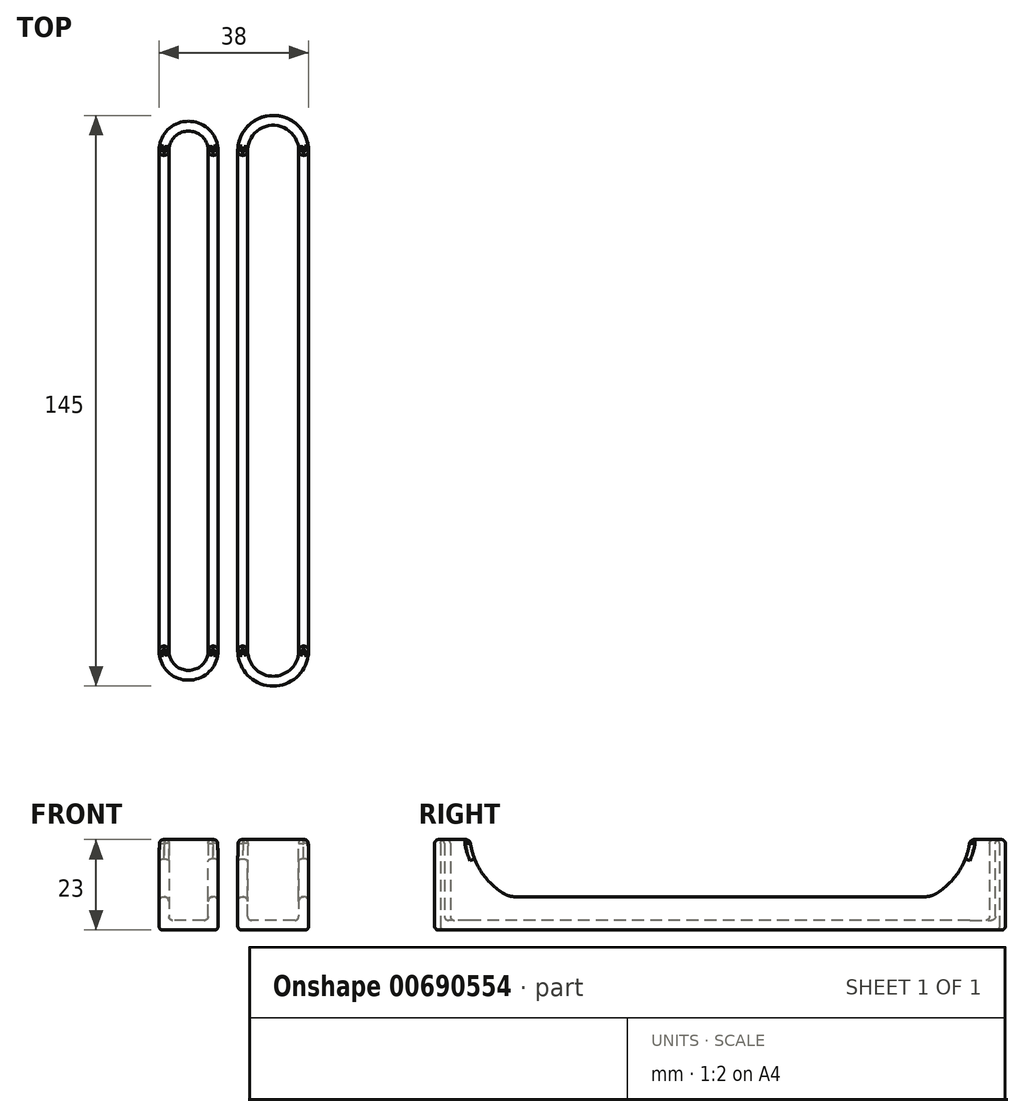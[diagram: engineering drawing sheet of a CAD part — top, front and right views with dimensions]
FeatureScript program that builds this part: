
annotation { "Feature Type Name" : "Feature", "Feature Type Description" : "" }
export const myFeature = defineFeature(function(context is Context, id is Id, definition is map)
    precondition{}
    {
        {
            var Q0;
            Q0=qCreatedBy(makeId("Top.planeOp"),FACE);
            var sketch = newSketch(context, id + "F0", { "sketchPlane" : qUnion([Q0])});
            skLineSegment(sketch, "E0.left", {"start": v(-27.24, 46.28) * mm, "end": v(-27.24, -80.72) * mm});
            skLineSegment(sketch, "E0.right", {"start": v(-12.24, 46.28) * mm, "end": v(-12.24, -80.72) * mm});
            skLineSegment(sketch, "E1.left", {"start": v(-7.24, 46.28) * mm, "end": v(-7.24, -80.72) * mm});
            skLineSegment(sketch, "E1.right", {"start": v(10.76, 46.28) * mm, "end": v(10.76, -80.72) * mm});
            skArc(sketch, "E2", {"start": v(-27.24, -80.72) * mm, "mid": v(-19.74, -88.22) * mm, "end": v(-12.24, -80.72) * mm});
            skArc(sketch, "E3", {"start": v(-12.24, 46.28) * mm, "mid": v(-19.74, 53.78) * mm, "end": v(-27.24, 46.28) * mm});
            skArc(sketch, "E4", {"start": v(10.76, 46.28) * mm, "mid": v(1.76, 55.28) * mm, "end": v(-7.24, 46.28) * mm});
            skArc(sketch, "E5", {"start": v(-7.24, -80.72) * mm, "mid": v(1.76, -89.72) * mm, "end": v(10.76, -80.72) * mm});
            skSolve(sketch);
        }
        {
            var Q0;
            Q0=makeQuery(id+"F0.imprint","IMPRINT",FACE,{"disambiguationData":[TD([[makeQuery(id+"F0.imprint","IMPRINT",EDGE,{"derivedFrom":sQuery(id+"F0.wireOp",EDGE,"E1.left")}),1.0]])]});
            var Q1;
            Q1=makeQuery(id+"F0.imprint","IMPRINT",FACE,{"disambiguationData":[TD([[makeQuery(id+"F0.imprint","IMPRINT",EDGE,{"derivedFrom":sQuery(id+"F0.wireOp",EDGE,"E0.left")}),1.0]])]});
            extrude(context, id + "F1", {"entities" : qUnion([Q0, Q1]), "depth" : 23 * mm, "offsetDistance" : 25 * mm});
        }
        {
            var Q0;
            Q0=makeQuery(id+"F1.opExtrude","CAP_FACE",FACE,{"disambiguationData":[OSD([sQuery(id+"F0.wireOp",EDGE,"E0.left"),sQuery(id+"F0.wireOp",EDGE,"E0.right"),sQuery(id+"F0.wireOp",EDGE,"E2"),sQuery(id+"F0.wireOp",EDGE,"E3")])],"isStart":false});
            var Q1;
            Q1=makeQuery(id+"F1.opExtrude","CAP_FACE",FACE,{"disambiguationData":[OSD([sQuery(id+"F0.wireOp",EDGE,"E1.left"),sQuery(id+"F0.wireOp",EDGE,"E1.right"),sQuery(id+"F0.wireOp",EDGE,"E4"),sQuery(id+"F0.wireOp",EDGE,"E5")])],"isStart":false});
            shell(context, id + "F2", {"entities" : qUnion([Q0, Q1]), "thickness" : 2.5 * mm});
        }
        {
            var Q0;
            Q0=makeQuery(id+"F1.opExtrude","CAP_EDGE",EDGE,{"disambiguationData":[OSD([sQuery(id+"F0.wireOp",EDGE,"E2")])],"isStart":false});
            var Q1;
            Q1=makeQuery(id+"F1.opExtrude","CAP_EDGE",EDGE,{"disambiguationData":[OSD([sQuery(id+"F0.wireOp",EDGE,"E0.right")])],"isStart":true});
            var Q2;
            Q2=makeQuery(id+"F1.opExtrude","CAP_EDGE",EDGE,{"disambiguationData":[OSD([sQuery(id+"F0.wireOp",EDGE,"E0.right")])],"isStart":false});
            var Q3;
            {var subQ0=sQuery(id+"F0.wireOp",EDGE,"E0.right");Q3=makeQuery(id+"F2.opShell","OFFSET_EDGE",EDGE,{"disambiguationData":[OSD([subQ0]),TDD([makeQuery(id+"F1.opExtrude","CAP_EDGE",EDGE,{"disambiguationData":[OSD([subQ0])],"isStart":false})])]});}
            var Q4;
            {var subQ0=sQuery(id+"F0.wireOp",EDGE,"E2");Q4=makeQuery(id+"F2.opShell","OFFSET_EDGE",EDGE,{"disambiguationData":[OSD([subQ0]),TDD([makeQuery(id+"F1.opExtrude","CAP_EDGE",EDGE,{"disambiguationData":[OSD([subQ0])],"isStart":false})])]});}
            var Q5;
            {var subQ0=sQuery(id+"F0.wireOp",EDGE,"E0.left");Q5=makeQuery(id+"F2.opShell","OFFSET_EDGE",EDGE,{"disambiguationData":[OSD([subQ0]),TDD([makeQuery(id+"F1.opExtrude","CAP_EDGE",EDGE,{"disambiguationData":[OSD([subQ0])],"isStart":false})])]});}
            var Q6;
            Q6=makeQuery(id+"F1.opExtrude","CAP_EDGE",EDGE,{"disambiguationData":[OSD([sQuery(id+"F0.wireOp",EDGE,"E0.left")])],"isStart":false});
            var Q7;
            {var subQ0=sQuery(id+"F0.wireOp",EDGE,"E3");Q7=makeQuery(id+"F2.opShell","OFFSET_EDGE",EDGE,{"disambiguationData":[OSD([subQ0]),TDD([makeQuery(id+"F1.opExtrude","CAP_EDGE",EDGE,{"disambiguationData":[OSD([subQ0])],"isStart":false})])]});}
            var Q8;
            Q8=makeQuery(id+"F1.opExtrude","CAP_EDGE",EDGE,{"disambiguationData":[OSD([sQuery(id+"F0.wireOp",EDGE,"E3")])],"isStart":false});
            var Q9;
            Q9=makeQuery(id+"F1.opExtrude","CAP_EDGE",EDGE,{"disambiguationData":[OSD([sQuery(id+"F0.wireOp",EDGE,"E3")])],"isStart":true});
            var Q10;
            Q10=makeQuery(id+"F1.opExtrude","CAP_EDGE",EDGE,{"disambiguationData":[OSD([sQuery(id+"F0.wireOp",EDGE,"E0.left")])],"isStart":true});
            var Q11;
            Q11=makeQuery(id+"F1.opExtrude","CAP_EDGE",EDGE,{"disambiguationData":[OSD([sQuery(id+"F0.wireOp",EDGE,"E2")])],"isStart":true});
            var Q12;
            {var subQ0=sQuery(id+"F0.wireOp",EDGE,"E1.left");Q12=makeQuery(id+"F2.opShell","OFFSET_EDGE",EDGE,{"disambiguationData":[OSD([subQ0]),TDD([makeQuery(id+"F1.opExtrude","CAP_EDGE",EDGE,{"disambiguationData":[OSD([subQ0])],"isStart":false})])]});}
            var Q13;
            Q13=makeQuery(id+"F1.opExtrude","CAP_EDGE",EDGE,{"disambiguationData":[OSD([sQuery(id+"F0.wireOp",EDGE,"E1.left")])],"isStart":false});
            var Q14;
            {var subQ0=sQuery(id+"F0.wireOp",EDGE,"E1.right");Q14=makeQuery(id+"F2.opShell","OFFSET_EDGE",EDGE,{"disambiguationData":[OSD([subQ0]),TDD([makeQuery(id+"F1.opExtrude","CAP_EDGE",EDGE,{"disambiguationData":[OSD([subQ0])],"isStart":false})])]});}
            var Q15;
            Q15=makeQuery(id+"F1.opExtrude","CAP_EDGE",EDGE,{"disambiguationData":[OSD([sQuery(id+"F0.wireOp",EDGE,"E1.right")])],"isStart":false});
            var Q16;
            Q16=makeQuery(id+"F1.opExtrude","CAP_EDGE",EDGE,{"disambiguationData":[OSD([sQuery(id+"F0.wireOp",EDGE,"E5")])],"isStart":false});
            var Q17;
            {var subQ0=sQuery(id+"F0.wireOp",EDGE,"E5");Q17=makeQuery(id+"F2.opShell","OFFSET_EDGE",EDGE,{"disambiguationData":[OSD([subQ0]),TDD([makeQuery(id+"F1.opExtrude","CAP_EDGE",EDGE,{"disambiguationData":[OSD([subQ0])],"isStart":false})])]});}
            var Q18;
            {var subQ0=sQuery(id+"F0.wireOp",EDGE,"E4");Q18=makeQuery(id+"F2.opShell","OFFSET_EDGE",EDGE,{"disambiguationData":[OSD([subQ0]),TDD([makeQuery(id+"F1.opExtrude","CAP_EDGE",EDGE,{"disambiguationData":[OSD([subQ0])],"isStart":false})])]});}
            var Q19;
            Q19=makeQuery(id+"F1.opExtrude","CAP_EDGE",EDGE,{"disambiguationData":[OSD([sQuery(id+"F0.wireOp",EDGE,"E4")])],"isStart":false});
            var Q20;
            Q20=makeQuery(id+"F1.opExtrude","CAP_EDGE",EDGE,{"disambiguationData":[OSD([sQuery(id+"F0.wireOp",EDGE,"E5")])],"isStart":true});
            var Q21;
            Q21=makeQuery(id+"F1.opExtrude","CAP_EDGE",EDGE,{"disambiguationData":[OSD([sQuery(id+"F0.wireOp",EDGE,"E1.right")])],"isStart":true});
            var Q22;
            Q22=makeQuery(id+"F1.opExtrude","CAP_EDGE",EDGE,{"disambiguationData":[OSD([sQuery(id+"F0.wireOp",EDGE,"E4")])],"isStart":true});
            var Q23;
            Q23=makeQuery(id+"F1.opExtrude","CAP_EDGE",EDGE,{"disambiguationData":[OSD([sQuery(id+"F0.wireOp",EDGE,"E1.left")])],"isStart":true});
            var Q24;
            {var subQ0=sQuery(id+"F0.wireOp",EDGE,"E1.left");Q24=makeQuery(id+"F2.opShell","OFFSET_EDGE",EDGE,{"disambiguationData":[OSD([subQ0]),TDD([makeQuery(id+"F1.opExtrude","CAP_EDGE",EDGE,{"disambiguationData":[OSD([subQ0])],"isStart":true})])]});}
            var Q25;
            {var subQ0=sQuery(id+"F0.wireOp",EDGE,"E4");Q25=makeQuery(id+"F2.opShell","OFFSET_EDGE",EDGE,{"disambiguationData":[OSD([subQ0]),TDD([makeQuery(id+"F1.opExtrude","CAP_EDGE",EDGE,{"disambiguationData":[OSD([subQ0])],"isStart":true})])]});}
            var Q26;
            {var subQ0=sQuery(id+"F0.wireOp",EDGE,"E1.right");Q26=makeQuery(id+"F2.opShell","OFFSET_EDGE",EDGE,{"disambiguationData":[OSD([subQ0]),TDD([makeQuery(id+"F1.opExtrude","CAP_EDGE",EDGE,{"disambiguationData":[OSD([subQ0])],"isStart":true})])]});}
            var Q27;
            {var subQ0=sQuery(id+"F0.wireOp",EDGE,"E5");Q27=makeQuery(id+"F2.opShell","OFFSET_EDGE",EDGE,{"disambiguationData":[OSD([subQ0]),TDD([makeQuery(id+"F1.opExtrude","CAP_EDGE",EDGE,{"disambiguationData":[OSD([subQ0])],"isStart":true})])]});}
            var Q28;
            {var subQ0=sQuery(id+"F0.wireOp",EDGE,"E2");Q28=makeQuery(id+"F2.opShell","OFFSET_EDGE",EDGE,{"disambiguationData":[OSD([subQ0]),TDD([makeQuery(id+"F1.opExtrude","CAP_EDGE",EDGE,{"disambiguationData":[OSD([subQ0])],"isStart":true})])]});}
            var Q29;
            {var subQ0=sQuery(id+"F0.wireOp",EDGE,"E0.right");Q29=makeQuery(id+"F2.opShell","OFFSET_EDGE",EDGE,{"disambiguationData":[OSD([subQ0]),TDD([makeQuery(id+"F1.opExtrude","CAP_EDGE",EDGE,{"disambiguationData":[OSD([subQ0])],"isStart":true})])]});}
            var Q30;
            {var subQ0=sQuery(id+"F0.wireOp",EDGE,"E3");Q30=makeQuery(id+"F2.opShell","OFFSET_EDGE",EDGE,{"disambiguationData":[OSD([subQ0]),TDD([makeQuery(id+"F1.opExtrude","CAP_EDGE",EDGE,{"disambiguationData":[OSD([subQ0])],"isStart":true})])]});}
            var Q31;
            {var subQ0=sQuery(id+"F0.wireOp",EDGE,"E0.left");Q31=makeQuery(id+"F2.opShell","OFFSET_EDGE",EDGE,{"disambiguationData":[OSD([subQ0]),TDD([makeQuery(id+"F1.opExtrude","CAP_EDGE",EDGE,{"disambiguationData":[OSD([subQ0])],"isStart":true})])]});}
            fillet(context, id + "F3", {"entities" : qUnion([Q0, Q1, Q2, Q3, Q4, Q5, Q6, Q7, Q8, Q9, Q10, Q11, Q12, Q13, Q14, Q15, Q16, Q17, Q18, Q19, Q20, Q21, Q22, Q23, Q24, Q25, Q26, Q27, Q28, Q29, Q30, Q31]), "radius" : 1 * mm, "tangentPropagation" : true, "allowEdgeOverflow" : false});
        }
        {
            var Q0;
            Q0=makeQuery(id+"F1.opExtrude","SWEPT_FACE",FACE,{"disambiguationData":[OSD([sQuery(id+"F0.wireOp",EDGE,"E1.right")])]});
            var sketch = newSketch(context, id + "F4", { "sketchPlane" : qUnion([Q0])});
            skLineSegment(sketch, "E6", {"start": v(-80.72, 23) * mm, "end": v(46.28, 23) * mm});
            skLineSegment(sketch, "E7", {"start": v(35.02, 8.5) * mm, "end": v(-69.46, 8.5) * mm});
            skArc(sketch, "E8", {"start": v(-80.72, 23) * mm, "mid": v(-78.02, 15.06) * mm, "end": v(-72.02, 9.2) * mm});
            skArc(sketch, "E9", {"start": v(37.59, 9.2) * mm, "mid": v(43.59, 15.06) * mm, "end": v(46.28, 23) * mm});
            skPoint(sketch, "E10.visualSharp", {"position": v(-70.72, 8.5) * mm});
            skArc(sketch, "E10.filletArc", {"start": v(-72.02, 9.2) * mm, "mid": v(-70.79, 8.68) * mm, "end": v(-69.46, 8.5) * mm});
            skPoint(sketch, "E11.visualSharp", {"position": v(36.28, 8.5) * mm});
            skArc(sketch, "E11.filletArc", {"start": v(35.02, 8.5) * mm, "mid": v(36.35, 8.68) * mm, "end": v(37.59, 9.2) * mm});
            skSolve(sketch);
        }
        {
            var Q0;
            Q0 = qSketchRegion(id + "F4", true);
            extrude(context, id + "F5", {"entities" : qUnion([Q0]), "operationType" : NewBodyOperationType.REMOVE, "oppositeDirection" : true, "depth" : 70.7 * mm, "offsetDistance" : 25 * mm});
        }
        {
            var Q0;
            {var subQ0=sQuery(id+"F0.wireOp",EDGE,"E1.right");var subQ1=makeQuery(id+"F1.opExtrude","CAP_EDGE",EDGE,{"disambiguationData":[OSD([subQ0])],"isStart":false});var subQ2=sQuery(id+"F0.wireOp",EDGE,"E5");var subQ4=makeQuery(id+"F1.opExtrude","CAP_FACE",FACE,{"disambiguationData":[OSD([sQuery(id+"F0.wireOp",EDGE,"E1.left"),subQ0,sQuery(id+"F0.wireOp",EDGE,"E4"),subQ2])],"isStart":false});var subQ5=sQuery(id+"F4.wireOp",EDGE,"E8");var subQ6=makeQuery(id+"F5.opExtrude","SWEPT_FACE",FACE,{"disambiguationData":[OSD([subQ5])]});Q0=makeQuery(id+"F5.boolean.opBoolean","COPY",EDGE,{"disambiguationData":[topologyDisambiguationEdgeConnected([subQ4,subQ6]),TD([makeQuery(id+"F3.opFillet","BLEND_FACE",FACE,{"disambiguationData":[OSD([subQ0]),TDD([subQ1])]})])],"derivedFrom":makeQuery(id+"F5.opExtrude","SWEPT_EDGE",EDGE,{"disambiguationData":[OSD([sQuery(id+"F4.wireOp",EDGE,"E6"),subQ5])]})});}
            var Q1;
            {var subQ0=sQuery(id+"F0.wireOp",EDGE,"E1.right");Q1=makeQuery(id+"F5.boolean.opBoolean","INTERSECT",EDGE,{"derivedFrom":[makeQuery(id+"F3.opFillet","BLEND_FACE",FACE,{"disambiguationData":[OSD([subQ0]),TDD([makeQuery(id+"F1.opExtrude","CAP_EDGE",EDGE,{"disambiguationData":[OSD([subQ0])],"isStart":false})])]}),makeQuery(id+"F5.opExtrude","SWEPT_FACE",FACE,{"disambiguationData":[OSD([sQuery(id+"F4.wireOp",EDGE,"E8")])]})]});}
            var Q2;
            {var subQ0=sQuery(id+"F0.wireOp",EDGE,"E1.right");Q2=makeQuery(id+"F5.boolean.opBoolean","INTERSECT",EDGE,{"derivedFrom":[makeQuery(id+"F3.opFillet","BLEND_FACE",FACE,{"disambiguationData":[OSD([subQ0]),TDD([makeQuery(id+"F2.opShell","OFFSET_EDGE",EDGE,{"disambiguationData":[OSD([subQ0]),TDD([makeQuery(id+"F1.opExtrude","CAP_EDGE",EDGE,{"disambiguationData":[OSD([subQ0])],"isStart":false})])]})])]}),makeQuery(id+"F5.opExtrude","SWEPT_FACE",FACE,{"disambiguationData":[OSD([sQuery(id+"F4.wireOp",EDGE,"E8")])]})]});}
            var Q3;
            {var subQ0=sQuery(id+"F0.wireOp",EDGE,"E1.left");Q3=makeQuery(id+"F5.boolean.opBoolean","INTERSECT",EDGE,{"derivedFrom":[makeQuery(id+"F3.opFillet","BLEND_FACE",FACE,{"disambiguationData":[OSD([subQ0]),TDD([makeQuery(id+"F2.opShell","OFFSET_EDGE",EDGE,{"disambiguationData":[OSD([subQ0]),TDD([makeQuery(id+"F1.opExtrude","CAP_EDGE",EDGE,{"disambiguationData":[OSD([subQ0])],"isStart":false})])]})])]}),makeQuery(id+"F5.opExtrude","SWEPT_FACE",FACE,{"disambiguationData":[OSD([sQuery(id+"F4.wireOp",EDGE,"E8")])]})]});}
            var Q4;
            {var subQ0=sQuery(id+"F0.wireOp",EDGE,"E1.left");var subQ1=makeQuery(id+"F1.opExtrude","CAP_EDGE",EDGE,{"disambiguationData":[OSD([subQ0])],"isStart":false});var subQ2=sQuery(id+"F0.wireOp",EDGE,"E5");var subQ4=sQuery(id+"F4.wireOp",EDGE,"E8");var subQ5=makeQuery(id+"F5.opExtrude","SWEPT_FACE",FACE,{"disambiguationData":[OSD([subQ4])]});var subQ6=makeQuery(id+"F1.opExtrude","CAP_FACE",FACE,{"disambiguationData":[OSD([subQ0,sQuery(id+"F0.wireOp",EDGE,"E1.right"),sQuery(id+"F0.wireOp",EDGE,"E4"),subQ2])],"isStart":false});Q4=makeQuery(id+"F5.boolean.opBoolean","COPY",EDGE,{"disambiguationData":[topologyDisambiguationEdgeConnected([subQ6,subQ5]),TD([makeQuery(id+"F3.opFillet","BLEND_FACE",FACE,{"disambiguationData":[OSD([subQ0]),TDD([subQ1])]})])],"derivedFrom":makeQuery(id+"F5.opExtrude","SWEPT_EDGE",EDGE,{"disambiguationData":[OSD([sQuery(id+"F4.wireOp",EDGE,"E6"),subQ4])]})});}
            var Q5;
            {var subQ0=sQuery(id+"F0.wireOp",EDGE,"E1.left");Q5=makeQuery(id+"F5.boolean.opBoolean","INTERSECT",EDGE,{"derivedFrom":[makeQuery(id+"F3.opFillet","BLEND_FACE",FACE,{"disambiguationData":[OSD([subQ0]),TDD([makeQuery(id+"F1.opExtrude","CAP_EDGE",EDGE,{"disambiguationData":[OSD([subQ0])],"isStart":false})])]}),makeQuery(id+"F5.opExtrude","SWEPT_FACE",FACE,{"disambiguationData":[OSD([sQuery(id+"F4.wireOp",EDGE,"E8")])]})]});}
            var Q6;
            {var subQ0=sQuery(id+"F0.wireOp",EDGE,"E0.right");var subQ1=makeQuery(id+"F1.opExtrude","CAP_EDGE",EDGE,{"disambiguationData":[OSD([subQ0])],"isStart":false});var subQ2=sQuery(id+"F0.wireOp",EDGE,"E2");var subQ4=makeQuery(id+"F1.opExtrude","CAP_FACE",FACE,{"disambiguationData":[OSD([sQuery(id+"F0.wireOp",EDGE,"E0.left"),subQ0,subQ2,sQuery(id+"F0.wireOp",EDGE,"E3")])],"isStart":false});var subQ5=sQuery(id+"F4.wireOp",EDGE,"E8");var subQ6=makeQuery(id+"F5.opExtrude","SWEPT_FACE",FACE,{"disambiguationData":[OSD([subQ5])]});Q6=makeQuery(id+"F5.boolean.opBoolean","COPY",EDGE,{"disambiguationData":[topologyDisambiguationEdgeConnected([subQ4,subQ6]),TD([makeQuery(id+"F3.opFillet","BLEND_FACE",FACE,{"disambiguationData":[OSD([subQ0]),TDD([subQ1])]})])],"derivedFrom":makeQuery(id+"F5.opExtrude","SWEPT_EDGE",EDGE,{"disambiguationData":[OSD([sQuery(id+"F4.wireOp",EDGE,"E6"),subQ5])]})});}
            var Q7;
            {var subQ0=sQuery(id+"F0.wireOp",EDGE,"E0.right");Q7=makeQuery(id+"F5.boolean.opBoolean","INTERSECT",EDGE,{"derivedFrom":[makeQuery(id+"F3.opFillet","BLEND_FACE",FACE,{"disambiguationData":[OSD([subQ0]),TDD([makeQuery(id+"F1.opExtrude","CAP_EDGE",EDGE,{"disambiguationData":[OSD([subQ0])],"isStart":false})])]}),makeQuery(id+"F5.opExtrude","SWEPT_FACE",FACE,{"disambiguationData":[OSD([sQuery(id+"F4.wireOp",EDGE,"E8")])]})]});}
            var Q8;
            {var subQ0=sQuery(id+"F0.wireOp",EDGE,"E0.right");Q8=makeQuery(id+"F5.boolean.opBoolean","INTERSECT",EDGE,{"derivedFrom":[makeQuery(id+"F3.opFillet","BLEND_FACE",FACE,{"disambiguationData":[OSD([subQ0]),TDD([makeQuery(id+"F2.opShell","OFFSET_EDGE",EDGE,{"disambiguationData":[OSD([subQ0]),TDD([makeQuery(id+"F1.opExtrude","CAP_EDGE",EDGE,{"disambiguationData":[OSD([subQ0])],"isStart":false})])]})])]}),makeQuery(id+"F5.opExtrude","SWEPT_FACE",FACE,{"disambiguationData":[OSD([sQuery(id+"F4.wireOp",EDGE,"E8")])]})]});}
            var Q9;
            {var subQ0=sQuery(id+"F0.wireOp",EDGE,"E0.left");var subQ1=makeQuery(id+"F1.opExtrude","CAP_EDGE",EDGE,{"disambiguationData":[OSD([subQ0])],"isStart":false});var subQ2=sQuery(id+"F0.wireOp",EDGE,"E2");var subQ4=makeQuery(id+"F1.opExtrude","CAP_FACE",FACE,{"disambiguationData":[OSD([subQ0,sQuery(id+"F0.wireOp",EDGE,"E0.right"),subQ2,sQuery(id+"F0.wireOp",EDGE,"E3")])],"isStart":false});var subQ5=sQuery(id+"F4.wireOp",EDGE,"E8");var subQ6=makeQuery(id+"F5.opExtrude","SWEPT_FACE",FACE,{"disambiguationData":[OSD([subQ5])]});Q9=makeQuery(id+"F5.boolean.opBoolean","COPY",EDGE,{"disambiguationData":[topologyDisambiguationEdgeConnected([subQ4,subQ6]),TD([makeQuery(id+"F3.opFillet","BLEND_FACE",FACE,{"disambiguationData":[OSD([subQ0]),TDD([subQ1])]})])],"derivedFrom":makeQuery(id+"F5.opExtrude","SWEPT_EDGE",EDGE,{"disambiguationData":[OSD([sQuery(id+"F4.wireOp",EDGE,"E6"),subQ5])]})});}
            var Q10;
            {var subQ0=sQuery(id+"F0.wireOp",EDGE,"E0.left");Q10=makeQuery(id+"F5.boolean.opBoolean","INTERSECT",EDGE,{"derivedFrom":[makeQuery(id+"F3.opFillet","BLEND_FACE",FACE,{"disambiguationData":[OSD([subQ0]),TDD([makeQuery(id+"F2.opShell","OFFSET_EDGE",EDGE,{"disambiguationData":[OSD([subQ0]),TDD([makeQuery(id+"F1.opExtrude","CAP_EDGE",EDGE,{"disambiguationData":[OSD([subQ0])],"isStart":false})])]})])]}),makeQuery(id+"F5.opExtrude","SWEPT_FACE",FACE,{"disambiguationData":[OSD([sQuery(id+"F4.wireOp",EDGE,"E8")])]})]});}
            var Q11;
            {var subQ0=sQuery(id+"F0.wireOp",EDGE,"E0.left");Q11=makeQuery(id+"F5.boolean.opBoolean","INTERSECT",EDGE,{"derivedFrom":[makeQuery(id+"F3.opFillet","BLEND_FACE",FACE,{"disambiguationData":[OSD([subQ0]),TDD([makeQuery(id+"F1.opExtrude","CAP_EDGE",EDGE,{"disambiguationData":[OSD([subQ0])],"isStart":false})])]}),makeQuery(id+"F5.opExtrude","SWEPT_FACE",FACE,{"disambiguationData":[OSD([sQuery(id+"F4.wireOp",EDGE,"E8")])]})]});}
            var Q12;
            {var subQ0=sQuery(id+"F0.wireOp",EDGE,"E0.left");Q12=makeQuery(id+"F5.boolean.opBoolean","INTERSECT",EDGE,{"derivedFrom":[makeQuery(id+"F3.opFillet","BLEND_FACE",FACE,{"disambiguationData":[OSD([subQ0]),TDD([makeQuery(id+"F1.opExtrude","CAP_EDGE",EDGE,{"disambiguationData":[OSD([subQ0])],"isStart":false})])]}),makeQuery(id+"F5.opExtrude","SWEPT_FACE",FACE,{"disambiguationData":[OSD([sQuery(id+"F4.wireOp",EDGE,"E9")])]})]});}
            var Q13;
            {var subQ0=sQuery(id+"F0.wireOp",EDGE,"E0.left");var subQ1=makeQuery(id+"F1.opExtrude","CAP_EDGE",EDGE,{"disambiguationData":[OSD([subQ0])],"isStart":false});var subQ2=sQuery(id+"F4.wireOp",EDGE,"E9");var subQ3=makeQuery(id+"F5.opExtrude","SWEPT_FACE",FACE,{"disambiguationData":[OSD([subQ2])]});var subQ4=sQuery(id+"F0.wireOp",EDGE,"E3");var subQ6=makeQuery(id+"F1.opExtrude","CAP_FACE",FACE,{"disambiguationData":[OSD([subQ0,sQuery(id+"F0.wireOp",EDGE,"E0.right"),sQuery(id+"F0.wireOp",EDGE,"E2"),subQ4])],"isStart":false});Q13=makeQuery(id+"F5.boolean.opBoolean","COPY",EDGE,{"disambiguationData":[topologyDisambiguationEdgeConnected([subQ6,subQ3]),TD([makeQuery(id+"F3.opFillet","BLEND_FACE",FACE,{"disambiguationData":[OSD([subQ0]),TDD([subQ1])]})])],"derivedFrom":makeQuery(id+"F5.opExtrude","SWEPT_EDGE",EDGE,{"disambiguationData":[OSD([sQuery(id+"F4.wireOp",EDGE,"E6"),subQ2])]})});}
            var Q14;
            {var subQ0=sQuery(id+"F0.wireOp",EDGE,"E0.left");Q14=makeQuery(id+"F5.boolean.opBoolean","INTERSECT",EDGE,{"derivedFrom":[makeQuery(id+"F3.opFillet","BLEND_FACE",FACE,{"disambiguationData":[OSD([subQ0]),TDD([makeQuery(id+"F2.opShell","OFFSET_EDGE",EDGE,{"disambiguationData":[OSD([subQ0]),TDD([makeQuery(id+"F1.opExtrude","CAP_EDGE",EDGE,{"disambiguationData":[OSD([subQ0])],"isStart":false})])]})])]}),makeQuery(id+"F5.opExtrude","SWEPT_FACE",FACE,{"disambiguationData":[OSD([sQuery(id+"F4.wireOp",EDGE,"E9")])]})]});}
            var Q15;
            {var subQ0=sQuery(id+"F0.wireOp",EDGE,"E0.right");Q15=makeQuery(id+"F5.boolean.opBoolean","INTERSECT",EDGE,{"derivedFrom":[makeQuery(id+"F3.opFillet","BLEND_FACE",FACE,{"disambiguationData":[OSD([subQ0]),TDD([makeQuery(id+"F2.opShell","OFFSET_EDGE",EDGE,{"disambiguationData":[OSD([subQ0]),TDD([makeQuery(id+"F1.opExtrude","CAP_EDGE",EDGE,{"disambiguationData":[OSD([subQ0])],"isStart":false})])]})])]}),makeQuery(id+"F5.opExtrude","SWEPT_FACE",FACE,{"disambiguationData":[OSD([sQuery(id+"F4.wireOp",EDGE,"E9")])]})]});}
            var Q16;
            {var subQ0=sQuery(id+"F0.wireOp",EDGE,"E0.right");var subQ1=makeQuery(id+"F1.opExtrude","CAP_EDGE",EDGE,{"disambiguationData":[OSD([subQ0])],"isStart":false});var subQ2=sQuery(id+"F0.wireOp",EDGE,"E3");var subQ4=makeQuery(id+"F1.opExtrude","CAP_FACE",FACE,{"disambiguationData":[OSD([sQuery(id+"F0.wireOp",EDGE,"E0.left"),subQ0,sQuery(id+"F0.wireOp",EDGE,"E2"),subQ2])],"isStart":false});var subQ5=sQuery(id+"F4.wireOp",EDGE,"E9");var subQ6=makeQuery(id+"F5.opExtrude","SWEPT_FACE",FACE,{"disambiguationData":[OSD([subQ5])]});Q16=makeQuery(id+"F5.boolean.opBoolean","COPY",EDGE,{"disambiguationData":[topologyDisambiguationEdgeConnected([subQ4,subQ6]),TD([makeQuery(id+"F3.opFillet","BLEND_FACE",FACE,{"disambiguationData":[OSD([subQ0]),TDD([subQ1])]})])],"derivedFrom":makeQuery(id+"F5.opExtrude","SWEPT_EDGE",EDGE,{"disambiguationData":[OSD([sQuery(id+"F4.wireOp",EDGE,"E6"),subQ5])]})});}
            var Q17;
            {var subQ0=sQuery(id+"F0.wireOp",EDGE,"E0.right");Q17=makeQuery(id+"F5.boolean.opBoolean","INTERSECT",EDGE,{"derivedFrom":[makeQuery(id+"F3.opFillet","BLEND_FACE",FACE,{"disambiguationData":[OSD([subQ0]),TDD([makeQuery(id+"F1.opExtrude","CAP_EDGE",EDGE,{"disambiguationData":[OSD([subQ0])],"isStart":false})])]}),makeQuery(id+"F5.opExtrude","SWEPT_FACE",FACE,{"disambiguationData":[OSD([sQuery(id+"F4.wireOp",EDGE,"E9")])]})]});}
            var Q18;
            {var subQ0=sQuery(id+"F0.wireOp",EDGE,"E1.left");Q18=makeQuery(id+"F5.boolean.opBoolean","INTERSECT",EDGE,{"derivedFrom":[makeQuery(id+"F3.opFillet","BLEND_FACE",FACE,{"disambiguationData":[OSD([subQ0]),TDD([makeQuery(id+"F1.opExtrude","CAP_EDGE",EDGE,{"disambiguationData":[OSD([subQ0])],"isStart":false})])]}),makeQuery(id+"F5.opExtrude","SWEPT_FACE",FACE,{"disambiguationData":[OSD([sQuery(id+"F4.wireOp",EDGE,"E9")])]})]});}
            var Q19;
            {var subQ0=sQuery(id+"F0.wireOp",EDGE,"E1.left");var subQ1=makeQuery(id+"F1.opExtrude","CAP_EDGE",EDGE,{"disambiguationData":[OSD([subQ0])],"isStart":false});var subQ2=sQuery(id+"F0.wireOp",EDGE,"E4");var subQ4=makeQuery(id+"F1.opExtrude","CAP_FACE",FACE,{"disambiguationData":[OSD([subQ0,sQuery(id+"F0.wireOp",EDGE,"E1.right"),subQ2,sQuery(id+"F0.wireOp",EDGE,"E5")])],"isStart":false});var subQ5=sQuery(id+"F4.wireOp",EDGE,"E9");var subQ6=makeQuery(id+"F5.opExtrude","SWEPT_FACE",FACE,{"disambiguationData":[OSD([subQ5])]});Q19=makeQuery(id+"F5.boolean.opBoolean","COPY",EDGE,{"disambiguationData":[topologyDisambiguationEdgeConnected([subQ4,subQ6]),TD([makeQuery(id+"F3.opFillet","BLEND_FACE",FACE,{"disambiguationData":[OSD([subQ0]),TDD([subQ1])]})])],"derivedFrom":makeQuery(id+"F5.opExtrude","SWEPT_EDGE",EDGE,{"disambiguationData":[OSD([sQuery(id+"F4.wireOp",EDGE,"E6"),subQ5])]})});}
            var Q20;
            {var subQ0=sQuery(id+"F0.wireOp",EDGE,"E1.left");Q20=makeQuery(id+"F5.boolean.opBoolean","INTERSECT",EDGE,{"derivedFrom":[makeQuery(id+"F3.opFillet","BLEND_FACE",FACE,{"disambiguationData":[OSD([subQ0]),TDD([makeQuery(id+"F2.opShell","OFFSET_EDGE",EDGE,{"disambiguationData":[OSD([subQ0]),TDD([makeQuery(id+"F1.opExtrude","CAP_EDGE",EDGE,{"disambiguationData":[OSD([subQ0])],"isStart":false})])]})])]}),makeQuery(id+"F5.opExtrude","SWEPT_FACE",FACE,{"disambiguationData":[OSD([sQuery(id+"F4.wireOp",EDGE,"E9")])]})]});}
            var Q21;
            {var subQ0=sQuery(id+"F0.wireOp",EDGE,"E1.right");Q21=makeQuery(id+"F5.boolean.opBoolean","INTERSECT",EDGE,{"derivedFrom":[makeQuery(id+"F3.opFillet","BLEND_FACE",FACE,{"disambiguationData":[OSD([subQ0]),TDD([makeQuery(id+"F2.opShell","OFFSET_EDGE",EDGE,{"disambiguationData":[OSD([subQ0]),TDD([makeQuery(id+"F1.opExtrude","CAP_EDGE",EDGE,{"disambiguationData":[OSD([subQ0])],"isStart":false})])]})])]}),makeQuery(id+"F5.opExtrude","SWEPT_FACE",FACE,{"disambiguationData":[OSD([sQuery(id+"F4.wireOp",EDGE,"E9")])]})]});}
            var Q22;
            {var subQ0=sQuery(id+"F0.wireOp",EDGE,"E1.right");var subQ1=makeQuery(id+"F1.opExtrude","CAP_EDGE",EDGE,{"disambiguationData":[OSD([subQ0])],"isStart":false});var subQ2=sQuery(id+"F0.wireOp",EDGE,"E4");var subQ4=makeQuery(id+"F1.opExtrude","CAP_FACE",FACE,{"disambiguationData":[OSD([sQuery(id+"F0.wireOp",EDGE,"E1.left"),subQ0,subQ2,sQuery(id+"F0.wireOp",EDGE,"E5")])],"isStart":false});var subQ5=sQuery(id+"F4.wireOp",EDGE,"E9");var subQ6=makeQuery(id+"F5.opExtrude","SWEPT_FACE",FACE,{"disambiguationData":[OSD([subQ5])]});Q22=makeQuery(id+"F5.boolean.opBoolean","COPY",EDGE,{"disambiguationData":[topologyDisambiguationEdgeConnected([subQ4,subQ6]),TD([makeQuery(id+"F3.opFillet","BLEND_FACE",FACE,{"disambiguationData":[OSD([subQ0]),TDD([subQ1])]})])],"derivedFrom":makeQuery(id+"F5.opExtrude","SWEPT_EDGE",EDGE,{"disambiguationData":[OSD([sQuery(id+"F4.wireOp",EDGE,"E6"),subQ5])]})});}
            var Q23;
            {var subQ0=sQuery(id+"F0.wireOp",EDGE,"E1.right");Q23=makeQuery(id+"F5.boolean.opBoolean","INTERSECT",EDGE,{"derivedFrom":[makeQuery(id+"F3.opFillet","BLEND_FACE",FACE,{"disambiguationData":[OSD([subQ0]),TDD([makeQuery(id+"F1.opExtrude","CAP_EDGE",EDGE,{"disambiguationData":[OSD([subQ0])],"isStart":false})])]}),makeQuery(id+"F5.opExtrude","SWEPT_FACE",FACE,{"disambiguationData":[OSD([sQuery(id+"F4.wireOp",EDGE,"E9")])]})]});}
            fillet(context, id + "F6", {"entities" : qUnion([Q0, Q1, Q2, Q3, Q4, Q5, Q6, Q7, Q8, Q9, Q10, Q11, Q12, Q13, Q14, Q15, Q16, Q17, Q18, Q19, Q20, Q21, Q22, Q23]), "radius" : 1.25 * mm, "tangentPropagation" : true, "allowEdgeOverflow" : false});
        }
    });
